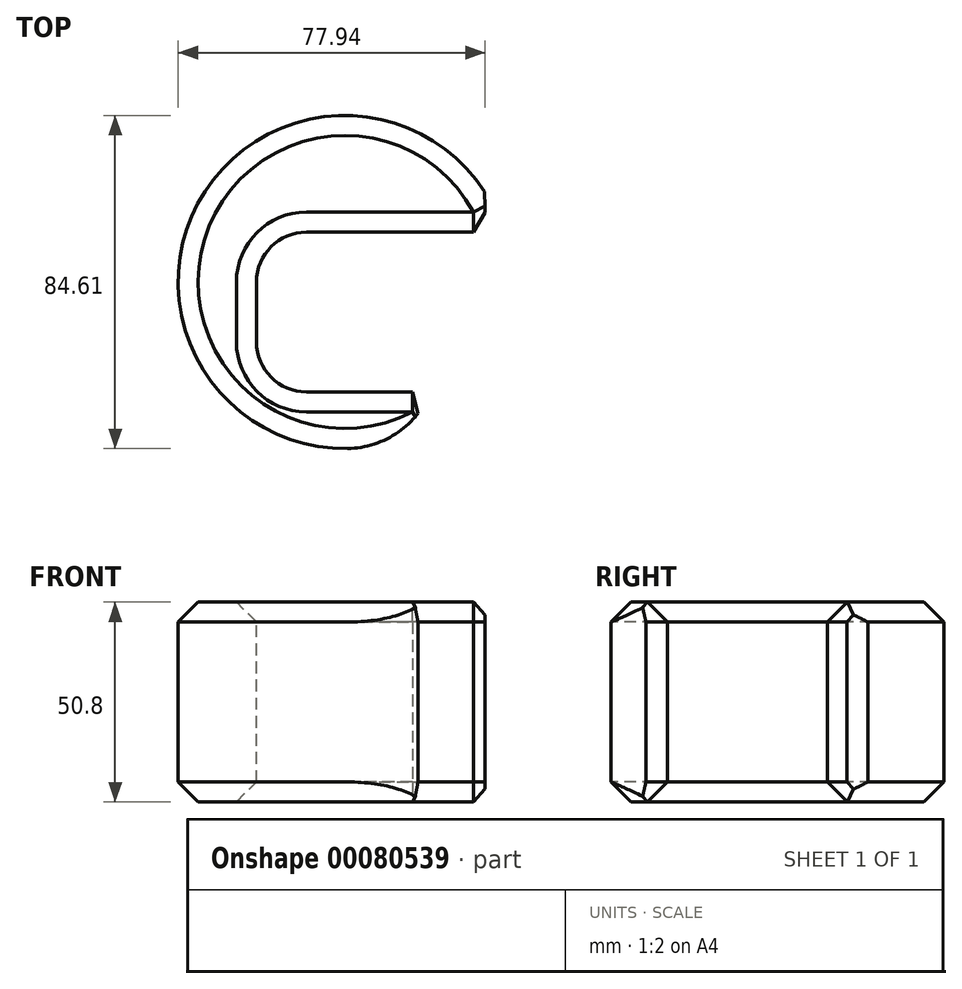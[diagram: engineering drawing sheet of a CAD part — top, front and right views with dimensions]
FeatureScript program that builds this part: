
annotation { "Feature Type Name" : "Feature", "Feature Type Description" : "" }
export const myFeature = defineFeature(function(context is Context, id is Id, definition is map)
    precondition{}
    {
        {
            var Q0;
            Q0=qCreatedBy(makeId("Top.planeOp"),FACE);
            var sketch = newSketch(context, id + "F0", { "sketchPlane" : qUnion([Q0])});
            skLineSegment(sketch, "E0.bottom", {"start": v(0, 0) * mm, "end": v(38.19, 0) * mm});
            skLineSegment(sketch, "E0.top", {"start": v(0, 24.01) * mm, "end": v(38.19, 24.01) * mm});
            skLineSegment(sketch, "E0.left", {"start": v(0, 0) * mm, "end": v(0, 24.01) * mm});
            skLineSegment(sketch, "E0.right", {"start": v(38.19, 0) * mm, "end": v(38.19, 24.01) * mm});
            skCircle(sketch, "E1", {"center": v(0, 0) * mm, "radius": 10.44 * mm});
            skLineSegment(sketch, "E2.bottom", {"start": v(0, 0) * mm, "end": v(-30.93, 0) * mm});
            skLineSegment(sketch, "E2.top", {"start": v(0, 24.01) * mm, "end": v(-30.93, 24.01) * mm});
            skLineSegment(sketch, "E2.right", {"start": v(-30.93, 0) * mm, "end": v(-30.93, 24.01) * mm});
            skLineSegment(sketch, "E3.top", {"start": v(0, -16.52) * mm, "end": v(-30.93, -16.52) * mm});
            skLineSegment(sketch, "E3.left", {"start": v(0, 0) * mm, "end": v(0, -16.52) * mm});
            skLineSegment(sketch, "E3.right", {"start": v(-30.93, 0) * mm, "end": v(-30.93, -16.52) * mm});
            skLineSegment(sketch, "E4.bottom", {"start": v(0, 0) * mm, "end": v(37.72, 0) * mm});
            skLineSegment(sketch, "E4.top", {"start": v(0, -16.52) * mm, "end": v(37.72, -16.52) * mm});
            skLineSegment(sketch, "E4.right", {"start": v(37.72, 0) * mm, "end": v(37.72, -16.52) * mm});
            skSolve(sketch);
        }
        {
            var Q0;
            {var subQ0=sQuery(id+"F0.wireOp",EDGE,"E0.left");var subQ1=sQuery(id+"F0.wireOp",EDGE,"E1");var subQ2=makeQuery(id+"F0.imprint","INTERSECT",VERTEX,{"derivedFrom":[subQ1,subQ0]});Q0=makeQuery(id+"F0.imprint","IMPRINT",FACE,{"disambiguationData":[TD([[makeQuery(id+"F0.imprint","IMPRINT",EDGE,{"disambiguationData":[TD([[subQ2,-1.0]])],"derivedFrom":subQ1}),1.0]])]});}
            var sketch = newSketch(context, id + "F1", { "sketchPlane" : qUnion([Q0])});
            skCircle(sketch, "E5", {"center": v(-63.26, 43.23) * mm, "radius": 19.64 * mm});
            skCircle(sketch, "E6", {"center": v(-8.67, 11.6) * mm, "radius": 42.3 * mm});
            skSolve(sketch);
        }
        {
            var Q0;
            {var subQ2=sQuery(id+"F0.wireOp",EDGE,"E2.top");Q0=makeQuery(id+"F0.imprint","IMPRINT",FACE,{"disambiguationData":[TD([[makeQuery(id+"F0.imprint","IMPRINT",EDGE,{"derivedFrom":subQ2}),1.0]])]});}
            extrude(context, id + "F2", {"entities" : qUnion([Q0]), "depth" : 25.4 * mm});
        }
        {
            var Q0;
            Q0=makeQuery(id+"F1.imprint","IMPRINT",FACE,{"disambiguationData":[TD([[makeQuery(id+"F1.imprint","IMPRINT",EDGE,{"derivedFrom":sQuery(id+"F1.wireOp",EDGE,"E6")}),1.0]])]});
            extrude(context, id + "F3", {"entities" : qUnion([Q0]), "operationType" : NewBodyOperationType.ADD, "depth" : 50.8 * mm});
        }
        {
            var Q0;
            Q0=makeQuery(id+"F3.opExtrude","CAP_FACE",FACE,{"disambiguationData":[OSD([sQuery(id+"F0.wireOp",EDGE,"E1"),sQuery(id+"F0.wireOp",EDGE,"E0.left"),sQuery(id+"F0.wireOp",EDGE,"E2.bottom"),sQuery(id+"F1.wireOp",EDGE,"E6")])],"isStart":false});
            var sketch = newSketch(context, id + "F4", { "sketchPlane" : qUnion([Q0])});
            skLineSegment(sketch, "E7.bottom", {"start": v(-31.1, 24.28) * mm, "end": v(39, 24.28) * mm});
            skLineSegment(sketch, "E7.top", {"start": v(-31.1, -16.3) * mm, "end": v(39, -16.3) * mm});
            skLineSegment(sketch, "E7.left", {"start": v(-31.1, 24.28) * mm, "end": v(-31.1, -16.3) * mm});
            skLineSegment(sketch, "E7.right", {"start": v(39, 24.28) * mm, "end": v(39, -16.3) * mm});
            skSolve(sketch);
        }
        {
            var Q0;
            Q0 = qSketchRegion(id + "F4", true);
            extrude(context, id + "F5", {"entities" : qUnion([Q0]), "operationType" : NewBodyOperationType.REMOVE, "oppositeDirection" : true, "depth" : 63.27 * mm});
        }
        {
            var Q0;
            Q0=makeQuery(id+"F5.boolean.opBoolean","COPY",EDGE,{"derivedFrom":makeQuery(id+"F5.opExtrude","SWEPT_EDGE",EDGE,{"disambiguationData":[OSD([sQuery(id+"F4.wireOp",EDGE,"E7.bottom"),sQuery(id+"F4.wireOp",EDGE,"E7.left")])]})});
            var Q1;
            Q1=makeQuery(id+"F5.boolean.opBoolean","COPY",EDGE,{"derivedFrom":makeQuery(id+"F5.opExtrude","SWEPT_EDGE",EDGE,{"disambiguationData":[OSD([sQuery(id+"F4.wireOp",EDGE,"E7.top"),sQuery(id+"F4.wireOp",EDGE,"E7.left")])]})});
            fillet(context, id + "F6", {"entities" : qUnion([Q0, Q1]), "radius" : 12.7 * mm, "tangentPropagation" : true, "allowEdgeOverflow" : false});
        }
        {
            var Q0;
            Q0=makeQuery(id+"F5.boolean.opBoolean","COPY",EDGE,{"derivedFrom":makeQuery(id+"F5.opExtrude","CAP_EDGE",EDGE,{"disambiguationData":[OSD([sQuery(id+"F4.wireOp",EDGE,"E7.bottom")])],"isStart":true})});
            var Q1;
            Q1=makeQuery(id+"F5.boolean.opBoolean","COPY",FACE,{"derivedFrom":makeQuery(id+"F5.opExtrude","SWEPT_FACE",FACE,{"disambiguationData":[OSD([sQuery(id+"F4.wireOp",EDGE,"E7.bottom")])]})});
            var Q2;
            Q2=makeQuery(id+"F3.opExtrude","CAP_EDGE",EDGE,{"disambiguationData":[OSD([sQuery(id+"F1.wireOp",EDGE,"E6")])],"isStart":false});
            var Q3;
            Q3=makeQuery(id+"F5.boolean.opBoolean","INTERSECT",EDGE,{"derivedFrom":[makeQuery(id+"F3.opExtrude","SWEPT_FACE",FACE,{"disambiguationData":[OSD([sQuery(id+"F1.wireOp",EDGE,"E6")])]}),makeQuery(id+"F5.opExtrude","SWEPT_FACE",FACE,{"disambiguationData":[OSD([sQuery(id+"F4.wireOp",EDGE,"E7.top")])]})]});
            var Q4;
            Q4=makeQuery(id+"F3.opExtrude","CAP_EDGE",EDGE,{"disambiguationData":[OSD([sQuery(id+"F1.wireOp",EDGE,"E6")])],"isStart":true});
            chamfer(context, id + "F7", {"entities" : qUnion([Q0, Q1, Q2, Q3, Q4]), "width" : 5.08 * mm, "tangentPropagation" : true});
        }
        {
            var Q0;
            {var subQ0=makeQuery(id+"F3.opExtrude","SWEPT_FACE",FACE,{"disambiguationData":[OSD([sQuery(id+"F1.wireOp",EDGE,"E6")])]});Q0=makeQuery(id+"F7.opChamfer","BLEND_EDGE",EDGE,{"blendedFrom":[makeQuery(id+"F5.boolean.opBoolean","INTERSECT",EDGE,{"derivedFrom":[subQ0,makeQuery(id+"F5.opExtrude","SWEPT_FACE",FACE,{"disambiguationData":[OSD([sQuery(id+"F4.wireOp",EDGE,"E7.top")])]})]}),subQ0],"blendedInto":[subQ0]});}
            var Q1;
            {var subQ0=makeQuery(id+"F3.opExtrude","SWEPT_FACE",FACE,{"disambiguationData":[OSD([sQuery(id+"F1.wireOp",EDGE,"E6")])]});Q1=makeQuery(id+"F7.opChamfer","BLEND_EDGE",EDGE,{"blendedFrom":[makeQuery(id+"F5.boolean.opBoolean","INTERSECT",EDGE,{"derivedFrom":[subQ0,makeQuery(id+"F5.opExtrude","SWEPT_FACE",FACE,{"disambiguationData":[OSD([sQuery(id+"F4.wireOp",EDGE,"E7.bottom")])]})]}),subQ0],"blendedInto":[subQ0]});}
            chamfer(context, id + "F8", {"entities" : qUnion([Q0, Q1]), "width" : 5.08 * mm, "tangentPropagation" : true});
        }
        {
            var Q0;
            {var subQ0=makeQuery(id+"F3.opExtrude","SWEPT_FACE",FACE,{"disambiguationData":[OSD([sQuery(id+"F1.wireOp",EDGE,"E6")])]});var subQ1=subQ0;Q0=makeQuery(id+"F8.opChamfer","BLEND_EDGE",EDGE,{"blendedFrom":[makeQuery(id+"F7.opChamfer","BLEND_EDGE",EDGE,{"blendedFrom":[makeQuery(id+"F5.boolean.opBoolean","INTERSECT",EDGE,{"derivedFrom":[subQ0,makeQuery(id+"F5.opExtrude","SWEPT_FACE",FACE,{"disambiguationData":[OSD([sQuery(id+"F4.wireOp",EDGE,"E7.top")])]})]}),subQ1],"blendedInto":[subQ1]}),subQ1],"blendedInto":[subQ1]});}
            fillet(context, id + "F9", {"entities" : qUnion([Q0]), "radius" : 23.27 * mm, "tangentPropagation" : true, "allowEdgeOverflow" : false});
        }
    });
